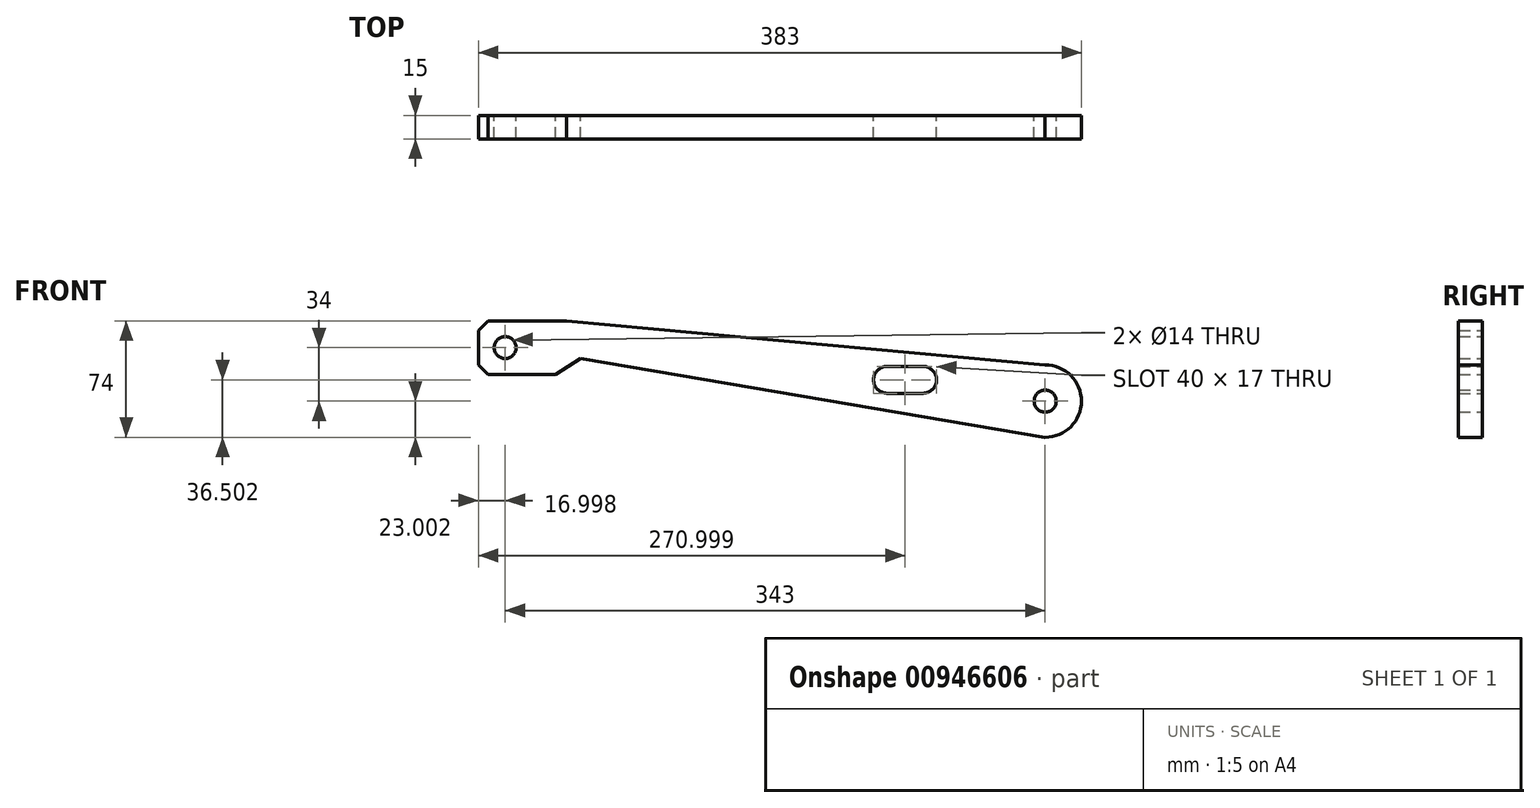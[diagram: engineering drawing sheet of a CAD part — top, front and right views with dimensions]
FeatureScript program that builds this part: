
annotation { "Feature Type Name" : "Feature", "Feature Type Description" : "" }
export const myFeature = defineFeature(function(context is Context, id is Id, definition is map)
    precondition{}
    {
        {
            var Q0;
            Q0=qCreatedBy(makeId("Front.planeOp"),FACE);
            var sketch = newSketch(context, id + "F0", { "sketchPlane" : qUnion([Q0])});
            skLineSegment(sketch, "E0", {"start": v(-18.85, 55.02) * mm, "end": v(-68.85, 55.02) * mm});
            skLineSegment(sketch, "E1", {"start": v(-68.85, 55.02) * mm, "end": v(-74.85, 49.02) * mm});
            skLineSegment(sketch, "E2", {"start": v(-74.85, 49.02) * mm, "end": v(-74.85, 27.02) * mm});
            skLineSegment(sketch, "E3", {"start": v(-74.85, 27.02) * mm, "end": v(-68.85, 21.02) * mm});
            skLineSegment(sketch, "E4", {"start": v(-68.85, 21.02) * mm, "end": v(-25.85, 21.02) * mm});
            skLineSegment(sketch, "E5", {"start": v(-25.85, 21.02) * mm, "end": v(-9.85, 31.02) * mm});
            skLineSegment(sketch, "E6", {"start": v(-9.85, 31.02) * mm, "end": v(285.15, -18.98) * mm});
            skCircle(sketch, "E7", {"center": v(285.15, 4.02) * mm, "radius": 7 * mm});
            skArc(sketch, "E8", {"start": v(285.15, -18.98) * mm, "mid": v(308.15, 4.02) * mm, "end": v(285.15, 27.02) * mm});
            skLineSegment(sketch, "E9", {"start": v(-18.85, 55.02) * mm, "end": v(285.15, 27.02) * mm});
            skCircle(sketch, "E10", {"center": v(-57.85, 38.02) * mm, "radius": 7 * mm});
            skPoint(sketch, "E10.centerSnap0", {"position": v(-74.85, 38.02) * mm});
            skLineSegment(sketch, "E11.bottom", {"start": v(184.65, 26.02) * mm, "end": v(207.65, 26.02) * mm});
            skLineSegment(sketch, "E11.top", {"start": v(184.65, 9.02) * mm, "end": v(207.65, 9.02) * mm});
            skLineSegment(sketch, "E11.left", {"start": v(176.15, 17.52) * mm, "end": v(176.15, 17.52) * mm});
            skLineSegment(sketch, "E11.right", {"start": v(216.15, 17.52) * mm, "end": v(216.15, 17.52) * mm});
            skPoint(sketch, "E12.visualSharp", {"position": v(176.15, 26.02) * mm});
            skArc(sketch, "E12.filletArc", {"start": v(184.65, 26.02) * mm, "mid": v(178.64, 23.53) * mm, "end": v(176.15, 17.52) * mm});
            skPoint(sketch, "E13.visualSharp", {"position": v(176.15, 9.02) * mm});
            skArc(sketch, "E13.filletArc", {"start": v(176.15, 17.52) * mm, "mid": v(178.64, 11.51) * mm, "end": v(184.65, 9.02) * mm});
            skPoint(sketch, "E14.visualSharp", {"position": v(216.15, 9.02) * mm});
            skArc(sketch, "E14.filletArc", {"start": v(207.65, 9.02) * mm, "mid": v(213.66, 11.51) * mm, "end": v(216.15, 17.52) * mm});
            skPoint(sketch, "E15.visualSharp", {"position": v(216.15, 26.02) * mm});
            skArc(sketch, "E15.filletArc", {"start": v(216.15, 17.52) * mm, "mid": v(213.66, 23.53) * mm, "end": v(207.65, 26.02) * mm});
            skSolve(sketch);
        }
        {
            var Q0;
            Q0 = qSketchRegion(id + "F0", true);
            extrude(context, id + "F1", {"entities" : qUnion([Q0]), "depth" : 15 * mm, "offsetDistance" : 25 * mm});
        }
    });
